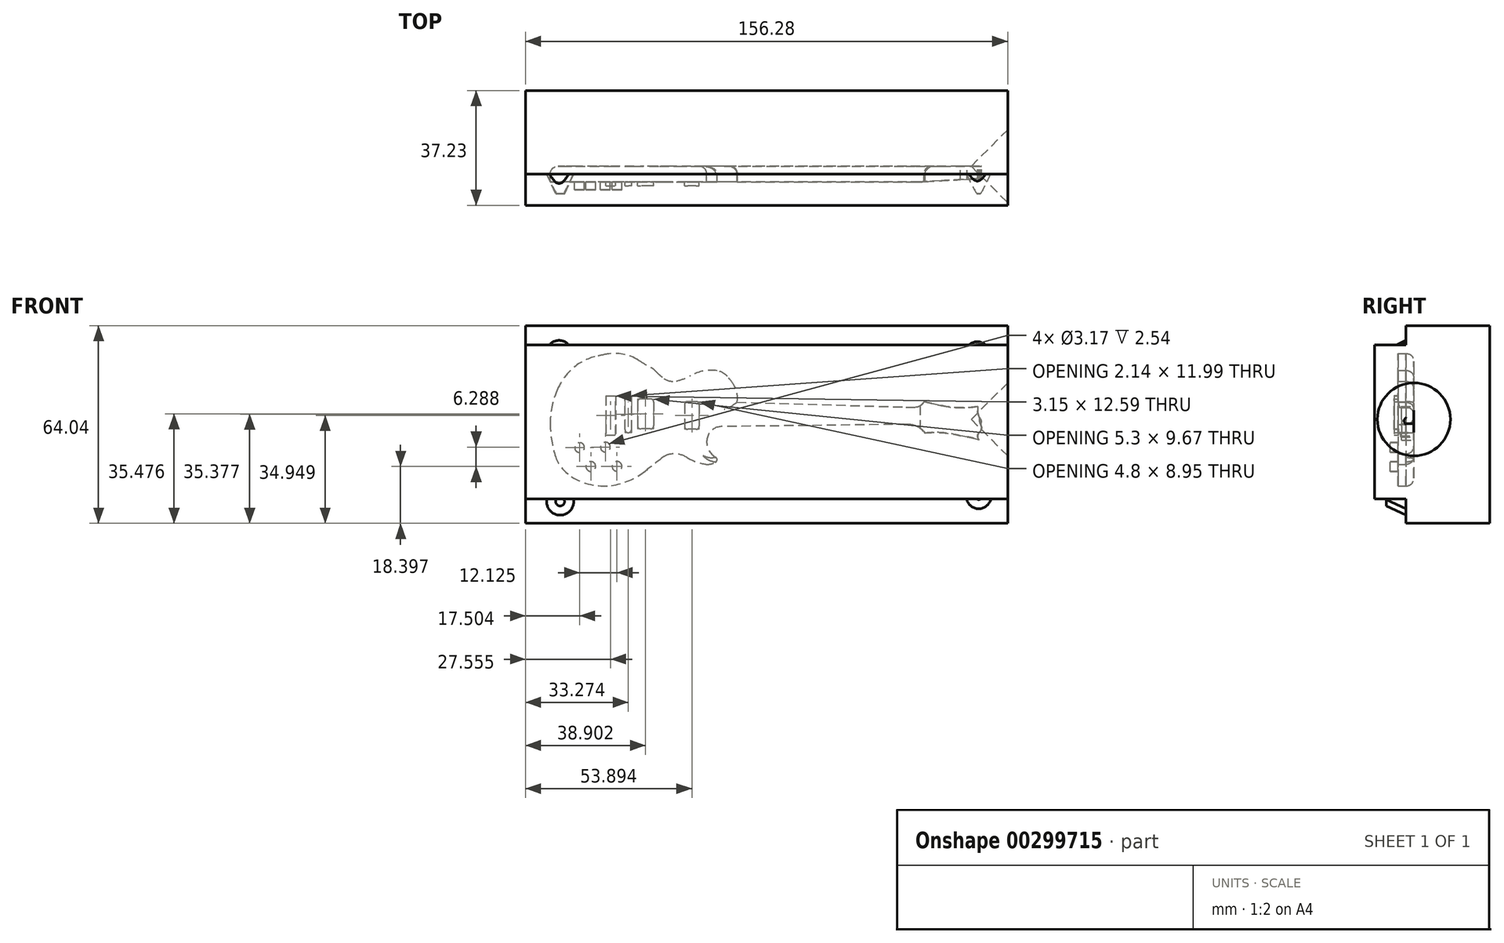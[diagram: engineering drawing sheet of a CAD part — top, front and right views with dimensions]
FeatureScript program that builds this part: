
annotation { "Feature Type Name" : "Feature", "Feature Type Description" : "" }
export const myFeature = defineFeature(function(context is Context, id is Id, definition is map)
    precondition{}
    {
        {
            var Q0;
            Q0=qCreatedBy(makeId("Front.planeOp"),FACE);
            var sketch = newSketch(context, id + "F0", { "sketchPlane" : qUnion([Q0])});
            skLineSegment(sketch, "E0", {"start": v(44.6, 23.47) * mm, "end": v(-15.58, 22.73) * mm});
            skArc(sketch, "E1", {"start": v(-15.58, 22.73) * mm, "mid": v(-18.3, 21.83) * mm, "end": v(-19.99, 19.52) * mm});
            skArc(sketch, "E2", {"start": v(-19.99, 19.52) * mm, "mid": v(-20.14, 16.5) * mm, "end": v(-18.7, 13.83) * mm});
            skArc(sketch, "E3", {"start": v(-18.7, 13.83) * mm, "mid": v(-18.05, 13.24) * mm, "end": v(-17.33, 12.73) * mm});
            skArc(sketch, "E4", {"start": v(-17.33, 12.73) * mm, "mid": v(-16.91, 12) * mm, "end": v(-17.33, 11.26) * mm});
            skArc(sketch, "E5", {"start": v(-17.33, 11.26) * mm, "mid": v(-19.1, 10.59) * mm, "end": v(-20.99, 10.58) * mm});
            skArc(sketch, "E6", {"start": v(-20.99, 10.58) * mm, "mid": v(-23.94, 11.4) * mm, "end": v(-26.69, 12.73) * mm});
            skArc(sketch, "E7", {"start": v(-26.69, 12.73) * mm, "mid": v(-29.2, 13.72) * mm, "end": v(-31.89, 13.83) * mm});
            skArc(sketch, "E8", {"start": v(-31.89, 13.83) * mm, "mid": v(-33.29, 13.46) * mm, "end": v(-34.54, 12.73) * mm});
            skArc(sketch, "E9", {"start": v(-34.54, 12.73) * mm, "mid": v(-37.37, 10.54) * mm, "end": v(-40.17, 8.33) * mm});
            skArc(sketch, "E10", {"start": v(-40.17, 8.33) * mm, "mid": v(-45.36, 5.24) * mm, "end": v(-51.18, 3.65) * mm});
            skArc(sketch, "E11", {"start": v(-51.18, 3.65) * mm, "mid": v(-57.9, 3.92) * mm, "end": v(-64.12, 6.5) * mm});
            skArc(sketch, "E12", {"start": v(-64.12, 6.5) * mm, "mid": v(-67.4, 9.5) * mm, "end": v(-69.44, 13.46) * mm});
            skArc(sketch, "E13", {"start": v(-69.44, 13.46) * mm, "mid": v(-70.63, 18.73) * mm, "end": v(-71, 24.1) * mm});
            skArc(sketch, "E14", {"start": v(-71, 24.1) * mm, "mid": v(-70.37, 29.65) * mm, "end": v(-68.62, 34.93) * mm});
            skArc(sketch, "E15", {"start": v(-68.62, 34.93) * mm, "mid": v(-66.86, 38.05) * mm, "end": v(-64.58, 40.8) * mm});
            skArc(sketch, "E16", {"start": v(-64.58, 40.8) * mm, "mid": v(-60.86, 43.66) * mm, "end": v(-56.5, 45.4) * mm});
            skArc(sketch, "E17", {"start": v(-56.5, 45.4) * mm, "mid": v(-54.54, 45.84) * mm, "end": v(-52.56, 46.22) * mm});
            skArc(sketch, "E18", {"start": v(-52.56, 46.22) * mm, "mid": v(-47.34, 46.17) * mm, "end": v(-42.47, 44.3) * mm});
            skArc(sketch, "E19", {"start": v(-42.47, 44.3) * mm, "mid": v(-40.37, 43.04) * mm, "end": v(-38.25, 41.82) * mm});
            skArc(sketch, "E20", {"start": v(-38.25, 41.82) * mm, "mid": v(-37.57, 41.36) * mm, "end": v(-36.96, 40.8) * mm});
            skArc(sketch, "E21", {"start": v(-36.96, 40.8) * mm, "mid": v(-35.6, 39.5) * mm, "end": v(-34.12, 38.33) * mm});
            skArc(sketch, "E22", {"start": v(-34.12, 38.33) * mm, "mid": v(-32.23, 37.5) * mm, "end": v(-30.17, 37.5) * mm});
            skArc(sketch, "E23", {"start": v(-30.17, 37.5) * mm, "mid": v(-27.76, 38.2) * mm, "end": v(-25.5, 39.25) * mm});
            skArc(sketch, "E24", {"start": v(-25.5, 39.25) * mm, "mid": v(-21.31, 40.75) * mm, "end": v(-16.87, 40.8) * mm});
            skArc(sketch, "E25", {"start": v(-16.87, 40.8) * mm, "mid": v(-15.11, 40.21) * mm, "end": v(-13.66, 39.06) * mm});
            skArc(sketch, "E26", {"start": v(-13.66, 39.06) * mm, "mid": v(-12.5, 37.64) * mm, "end": v(-11.45, 36.13) * mm});
            skArc(sketch, "E27", {"start": v(-11.45, 36.13) * mm, "mid": v(-10.43, 33.47) * mm, "end": v(-10.45, 30.62) * mm});
            skLineSegment(sketch, "E28", {"start": v(-10.45, 30.62) * mm, "end": v(44.33, 29.06) * mm});
            skArc(sketch, "E29", {"start": v(44.33, 29.06) * mm, "mid": v(45.89, 29.04) * mm, "end": v(47.45, 29.06) * mm});
            skArc(sketch, "E30", {"start": v(47.45, 29.06) * mm, "mid": v(49.03, 29.56) * mm, "end": v(50.1, 30.8) * mm});
            skLineSegment(sketch, "E31", {"start": v(50.1, 30.8) * mm, "end": v(55.8, 29.56) * mm});
            skPoint(sketch, "E31.endSnap0", {"position": v(49.03, 29.56) * mm});
            skArc(sketch, "E32", {"start": v(55.8, 29.56) * mm, "mid": v(61.65, 28.84) * mm, "end": v(67.54, 29.25) * mm});
            skLineSegment(sketch, "E33", {"start": v(67.54, 29.25) * mm, "end": v(67.54, 28) * mm});
            skArc(sketch, "E34", {"start": v(67.54, 28) * mm, "mid": v(67.78, 26.48) * mm, "end": v(68.47, 25.1) * mm});
            skArc(sketch, "E35", {"start": v(68.47, 25.1) * mm, "mid": v(68.7, 24.38) * mm, "end": v(68.47, 23.66) * mm});
            skLineSegment(sketch, "E36", {"start": v(68.47, 23.66) * mm, "end": v(68.7, 22.95) * mm});
            skPoint(sketch, "E36.endSnap0", {"position": v(68.7, 24.38) * mm});
            skArc(sketch, "E37", {"start": v(68.7, 22.95) * mm, "mid": v(68.72, 21.86) * mm, "end": v(68.15, 20.94) * mm});
            skArc(sketch, "E38", {"start": v(68.15, 20.94) * mm, "mid": v(67.53, 19.62) * mm, "end": v(68.08, 18.28) * mm});
            skLineSegment(sketch, "E39", {"start": v(68.08, 18.28) * mm, "end": v(66.46, 18.86) * mm});
            skArc(sketch, "E40", {"start": v(66.46, 18.86) * mm, "mid": v(65.3, 19.2) * mm, "end": v(64.12, 19.38) * mm});
            skArc(sketch, "E41", {"start": v(61.92, 19.77) * mm, "mid": v(56.25, 20.73) * mm, "end": v(50.5, 20.68) * mm});
            skLineSegment(sketch, "E42", {"start": v(64.12, 19.38) * mm, "end": v(61.92, 19.77) * mm});
            skArc(sketch, "E43", {"start": v(44.6, 23.47) * mm, "mid": v(47.87, 22.75) * mm, "end": v(50.5, 20.68) * mm});
            skPoint(sketch, "E44", {"position": v(-15.58, 22.73) * mm});
            skSolve(sketch);
        }
        {
            var Q0;
            Q0=qSketchRegion(id+"F0",true);
            extrude(context, id + "F1", {"entities" : qUnion([Q0]), "depth" : 5.08 * mm});
        }
        {
            var Q0;
            Q0=makeQuery(id+"F1.opExtrude","CAP_FACE",FACE,{"disambiguationData":[OSD([sQuery(id+"F0.wireOp",EDGE,"E0"),sQuery(id+"F0.wireOp",EDGE,"E1"),sQuery(id+"F0.wireOp",EDGE,"E2"),sQuery(id+"F0.wireOp",EDGE,"E3"),sQuery(id+"F0.wireOp",EDGE,"E4"),sQuery(id+"F0.wireOp",EDGE,"E5"),sQuery(id+"F0.wireOp",EDGE,"E6"),sQuery(id+"F0.wireOp",EDGE,"E7"),sQuery(id+"F0.wireOp",EDGE,"E8"),sQuery(id+"F0.wireOp",EDGE,"E9"),sQuery(id+"F0.wireOp",EDGE,"E10"),sQuery(id+"F0.wireOp",EDGE,"E11"),sQuery(id+"F0.wireOp",EDGE,"E12"),sQuery(id+"F0.wireOp",EDGE,"E13"),sQuery(id+"F0.wireOp",EDGE,"E14"),sQuery(id+"F0.wireOp",EDGE,"E15"),sQuery(id+"F0.wireOp",EDGE,"E16"),sQuery(id+"F0.wireOp",EDGE,"E17"),sQuery(id+"F0.wireOp",EDGE,"E18"),sQuery(id+"F0.wireOp",EDGE,"E19"),sQuery(id+"F0.wireOp",EDGE,"E20"),sQuery(id+"F0.wireOp",EDGE,"E21"),sQuery(id+"F0.wireOp",EDGE,"E22"),sQuery(id+"F0.wireOp",EDGE,"E23"),sQuery(id+"F0.wireOp",EDGE,"E24"),sQuery(id+"F0.wireOp",EDGE,"E25"),sQuery(id+"F0.wireOp",EDGE,"E26"),sQuery(id+"F0.wireOp",EDGE,"E27"),sQuery(id+"F0.wireOp",EDGE,"E28"),sQuery(id+"F0.wireOp",EDGE,"E29"),sQuery(id+"F0.wireOp",EDGE,"E30"),sQuery(id+"F0.wireOp",EDGE,"E31"),sQuery(id+"F0.wireOp",EDGE,"E32"),sQuery(id+"F0.wireOp",EDGE,"E33"),sQuery(id+"F0.wireOp",EDGE,"E34"),sQuery(id+"F0.wireOp",EDGE,"E35"),sQuery(id+"F0.wireOp",EDGE,"E36"),sQuery(id+"F0.wireOp",EDGE,"E37"),sQuery(id+"F0.wireOp",EDGE,"E38"),sQuery(id+"F0.wireOp",EDGE,"E39"),sQuery(id+"F0.wireOp",EDGE,"E40"),sQuery(id+"F0.wireOp",EDGE,"E41"),sQuery(id+"F0.wireOp",EDGE,"E42"),sQuery(id+"F0.wireOp",EDGE,"E43")])],"isStart":false});
            var sketch = newSketch(context, id + "F2", { "sketchPlane" : qUnion([Q0])});
            skLineSegment(sketch, "E45.bottom", {"start": v(-22.7, 30.81) * mm, "end": v(-27.5, 30.81) * mm});
            skLineSegment(sketch, "E45.top", {"start": v(-22.7, 21.87) * mm, "end": v(-27.5, 21.87) * mm});
            skLineSegment(sketch, "E45.left", {"start": v(-22.7, 30.81) * mm, "end": v(-22.7, 21.87) * mm});
            skLineSegment(sketch, "E45.right", {"start": v(-27.5, 30.81) * mm, "end": v(-27.5, 21.87) * mm});
            skLineSegment(sketch, "E46.bottom", {"start": v(-37.44, 31.7) * mm, "end": v(-42.74, 31.7) * mm});
            skLineSegment(sketch, "E46.top", {"start": v(-37.44, 22.03) * mm, "end": v(-42.74, 22.03) * mm});
            skLineSegment(sketch, "E46.left", {"start": v(-37.44, 31.7) * mm, "end": v(-37.44, 22.03) * mm});
            skLineSegment(sketch, "E46.right", {"start": v(-42.74, 31.7) * mm, "end": v(-42.74, 22.03) * mm});
            skLineSegment(sketch, "E47.bottom", {"start": v(-53, 32.63) * mm, "end": v(-49.86, 32.63) * mm});
            skLineSegment(sketch, "E47.top", {"start": v(-53, 20.04) * mm, "end": v(-49.86, 20.04) * mm});
            skLineSegment(sketch, "E47.left", {"start": v(-53, 32.63) * mm, "end": v(-53, 20.04) * mm});
            skLineSegment(sketch, "E47.right", {"start": v(-49.86, 32.63) * mm, "end": v(-49.86, 20.04) * mm});
            skLineSegment(sketch, "E48.bottom", {"start": v(-46.78, 20.77) * mm, "end": v(-44.65, 20.77) * mm});
            skLineSegment(sketch, "E48.top", {"start": v(-46.78, 32.76) * mm, "end": v(-44.65, 32.76) * mm});
            skLineSegment(sketch, "E48.left", {"start": v(-46.78, 20.77) * mm, "end": v(-46.78, 32.76) * mm});
            skLineSegment(sketch, "E48.right", {"start": v(-44.65, 20.77) * mm, "end": v(-44.65, 32.76) * mm});
            skSolve(sketch);
        }
        {
            var Q0;
            Q0=qSketchRegion(id+"F2",true);
            extrude(context, id + "F3", {"entities" : qUnion([Q0]), "operationType" : NewBodyOperationType.ADD, "depth" : 1.27 * mm});
        }
        {
            var Q0;
            Q0=makeQuery(id+"F2.imprint","IMPRINT",FACE,{"disambiguationData":[TD([[makeQuery(id+"F2.imprint","IMPRINT",EDGE,{"derivedFrom":sQuery(id+"F2.wireOp",EDGE,"E45.bottom")}),-1.0]])]});
            var sketch = newSketch(context, id + "F4", { "sketchPlane" : qUnion([Q0])});
            skCircle(sketch, "E49", {"center": v(-61.49, 15.93) * mm, "radius": 1.59 * mm});
            skPoint(sketch, "E49.first.point", {"position": v(-60.6, 17.25) * mm});
            skPoint(sketch, "E49.second.point", {"position": v(-63.06, 15.77) * mm});
            skPoint(sketch, "E49.third.point", {"position": v(-60.92, 14.45) * mm});
            skCircle(sketch, "E50", {"center": v(-53.12, 16.07) * mm, "radius": 1.59 * mm});
            skPoint(sketch, "E50.first.point", {"position": v(-54.4, 17.02) * mm});
            skPoint(sketch, "E50.second.point", {"position": v(-51.54, 16.26) * mm});
            skPoint(sketch, "E50.third.point", {"position": v(-51.7, 15.34) * mm});
            skCircle(sketch, "E51", {"center": v(-49.36, 9.85) * mm, "radius": 1.59 * mm});
            skPoint(sketch, "E51.first.point", {"position": v(-50.38, 11.07) * mm});
            skPoint(sketch, "E51.second.point", {"position": v(-48.35, 8.62) * mm});
            skPoint(sketch, "E51.third.point", {"position": v(-50.52, 8.76) * mm});
            skCircle(sketch, "E52", {"center": v(-57.85, 9.79) * mm, "radius": 1.59 * mm});
            skPoint(sketch, "E52.first.point", {"position": v(-57.26, 8.31) * mm});
            skPoint(sketch, "E52.second.point", {"position": v(-58.38, 11.29) * mm});
            skPoint(sketch, "E52.third.point", {"position": v(-59.42, 9.5) * mm});
            skSolve(sketch);
        }
        {
            var Q0;
            Q0=qSketchRegion(id+"F4",true);
            extrude(context, id + "F5", {"entities" : qUnion([Q0]), "operationType" : NewBodyOperationType.ADD, "depth" : 2.54 * mm});
        }
        {
            var Q0;
            Q0=makeQuery(id+"F1.opExtrude","CAP_EDGE",EDGE,{"disambiguationData":[OSD([sQuery(id+"F0.wireOp",EDGE,"E0")])],"isStart":true});
            var Q1;
            Q1=makeQuery(id+"F1.opExtrude","CAP_EDGE",EDGE,{"disambiguationData":[OSD([sQuery(id+"F0.wireOp",EDGE,"E28")])],"isStart":true});
            fillet(context, id + "F6", {"entities" : qUnion([Q0, Q1]), "radius" : 2.54 * mm, "tangentPropagation" : true, "allowEdgeOverflow" : false});
        }
        {
            var Q0;
            Q0=qCreatedBy(makeId("Top.planeOp"),FACE);
            var sketch = newSketch(context, id + "F7", { "sketchPlane" : qUnion([Q0])});
            skLineSegment(sketch, "E53", {"start": v(39.16, -5.62) * mm, "end": v(72.7, -3.75) * mm});
            skLineSegment(sketch, "E54", {"start": v(72.7, -3.75) * mm, "end": v(71.44, -9.77) * mm});
            skLineSegment(sketch, "E55", {"start": v(71.44, -9.77) * mm, "end": v(39.16, -5.62) * mm});
            skSolve(sketch);
        }
        {
            var Q0;
            Q0=makeQuery(id+"F7.imprint","IMPRINT",FACE,{"disambiguationData":[TD([[makeQuery(id+"F7.imprint","IMPRINT",EDGE,{"derivedFrom":sQuery(id+"F7.wireOp",EDGE,"E53")}),-1.0]])]});
            extrude(context, id + "F8", {"entities" : qUnion([Q0]), "operationType" : NewBodyOperationType.REMOVE, "depth" : 50.8 * mm});
        }
        {
            var Q0;
            Q0=makeQuery(id+"F3.opExtrude","SWEPT_EDGE",EDGE,{"disambiguationData":[OSD([sQuery(id+"F2.wireOp",EDGE,"E48.top"),sQuery(id+"F2.wireOp",EDGE,"E48.right")])]});
            var Q1;
            Q1=makeQuery(id+"F3.opExtrude","SWEPT_EDGE",EDGE,{"disambiguationData":[OSD([sQuery(id+"F2.wireOp",EDGE,"E48.top"),sQuery(id+"F2.wireOp",EDGE,"E48.left")])]});
            var Q2;
            Q2=makeQuery(id+"F3.opExtrude","SWEPT_EDGE",EDGE,{"disambiguationData":[OSD([sQuery(id+"F2.wireOp",EDGE,"E48.bottom"),sQuery(id+"F2.wireOp",EDGE,"E48.left")])]});
            var Q3;
            Q3=makeQuery(id+"F3.opExtrude","SWEPT_EDGE",EDGE,{"disambiguationData":[OSD([sQuery(id+"F2.wireOp",EDGE,"E48.bottom"),sQuery(id+"F2.wireOp",EDGE,"E48.right")])]});
            fillet(context, id + "F9", {"entities" : qUnion([Q0, Q1, Q2, Q3]), "radius" : 1.02 * mm, "tangentPropagation" : true, "allowEdgeOverflow" : false});
        }
        {
            var Q0;
            Q0=makeQuery(id+"F3.opExtrude","SWEPT_EDGE",EDGE,{"disambiguationData":[OSD([sQuery(id+"F2.wireOp",EDGE,"E46.bottom"),sQuery(id+"F2.wireOp",EDGE,"E46.left")])]});
            var Q1;
            Q1=makeQuery(id+"F3.opExtrude","SWEPT_EDGE",EDGE,{"disambiguationData":[OSD([sQuery(id+"F2.wireOp",EDGE,"E46.bottom"),sQuery(id+"F2.wireOp",EDGE,"E46.right")])]});
            var Q2;
            Q2=makeQuery(id+"F3.opExtrude","SWEPT_EDGE",EDGE,{"disambiguationData":[OSD([sQuery(id+"F2.wireOp",EDGE,"E46.top"),sQuery(id+"F2.wireOp",EDGE,"E46.right")])]});
            var Q3;
            Q3=makeQuery(id+"F3.opExtrude","SWEPT_EDGE",EDGE,{"disambiguationData":[OSD([sQuery(id+"F2.wireOp",EDGE,"E46.top"),sQuery(id+"F2.wireOp",EDGE,"E46.left")])]});
            var Q4;
            Q4=makeQuery(id+"F3.opExtrude","SWEPT_EDGE",EDGE,{"disambiguationData":[OSD([sQuery(id+"F2.wireOp",EDGE,"E45.top"),sQuery(id+"F2.wireOp",EDGE,"E45.left")])]});
            var Q5;
            Q5=makeQuery(id+"F3.opExtrude","SWEPT_EDGE",EDGE,{"disambiguationData":[OSD([sQuery(id+"F2.wireOp",EDGE,"E45.top"),sQuery(id+"F2.wireOp",EDGE,"E45.right")])]});
            var Q6;
            Q6=makeQuery(id+"F3.opExtrude","SWEPT_EDGE",EDGE,{"disambiguationData":[OSD([sQuery(id+"F2.wireOp",EDGE,"E45.bottom"),sQuery(id+"F2.wireOp",EDGE,"E45.right")])]});
            var Q7;
            Q7=makeQuery(id+"F3.opExtrude","SWEPT_EDGE",EDGE,{"disambiguationData":[OSD([sQuery(id+"F2.wireOp",EDGE,"E45.bottom"),sQuery(id+"F2.wireOp",EDGE,"E45.left")])]});
            fillet(context, id + "F10", {"entities" : qUnion([Q0, Q1, Q2, Q3, Q4, Q5, Q6, Q7]), "radius" : 1.02 * mm, "tangentPropagation" : true, "allowEdgeOverflow" : false});
        }
        {
            var Q0;
            Q0=makeQuery(id+"F1.opExtrude","CAP_FACE",FACE,{"disambiguationData":[OSD([sQuery(id+"F0.wireOp",EDGE,"E0"),sQuery(id+"F0.wireOp",EDGE,"E1"),sQuery(id+"F0.wireOp",EDGE,"E2"),sQuery(id+"F0.wireOp",EDGE,"E3"),sQuery(id+"F0.wireOp",EDGE,"E4"),sQuery(id+"F0.wireOp",EDGE,"E5"),sQuery(id+"F0.wireOp",EDGE,"E6"),sQuery(id+"F0.wireOp",EDGE,"E7"),sQuery(id+"F0.wireOp",EDGE,"E8"),sQuery(id+"F0.wireOp",EDGE,"E9"),sQuery(id+"F0.wireOp",EDGE,"E10"),sQuery(id+"F0.wireOp",EDGE,"E11"),sQuery(id+"F0.wireOp",EDGE,"E12"),sQuery(id+"F0.wireOp",EDGE,"E13"),sQuery(id+"F0.wireOp",EDGE,"E14"),sQuery(id+"F0.wireOp",EDGE,"E15"),sQuery(id+"F0.wireOp",EDGE,"E16"),sQuery(id+"F0.wireOp",EDGE,"E17"),sQuery(id+"F0.wireOp",EDGE,"E18"),sQuery(id+"F0.wireOp",EDGE,"E19"),sQuery(id+"F0.wireOp",EDGE,"E20"),sQuery(id+"F0.wireOp",EDGE,"E21"),sQuery(id+"F0.wireOp",EDGE,"E22"),sQuery(id+"F0.wireOp",EDGE,"E23"),sQuery(id+"F0.wireOp",EDGE,"E24"),sQuery(id+"F0.wireOp",EDGE,"E25"),sQuery(id+"F0.wireOp",EDGE,"E26"),sQuery(id+"F0.wireOp",EDGE,"E27"),sQuery(id+"F0.wireOp",EDGE,"E28"),sQuery(id+"F0.wireOp",EDGE,"E29"),sQuery(id+"F0.wireOp",EDGE,"E30"),sQuery(id+"F0.wireOp",EDGE,"E31"),sQuery(id+"F0.wireOp",EDGE,"E32"),sQuery(id+"F0.wireOp",EDGE,"E33"),sQuery(id+"F0.wireOp",EDGE,"E34"),sQuery(id+"F0.wireOp",EDGE,"E35"),sQuery(id+"F0.wireOp",EDGE,"E36"),sQuery(id+"F0.wireOp",EDGE,"E37"),sQuery(id+"F0.wireOp",EDGE,"E38"),sQuery(id+"F0.wireOp",EDGE,"E39"),sQuery(id+"F0.wireOp",EDGE,"E40"),sQuery(id+"F0.wireOp",EDGE,"E41"),sQuery(id+"F0.wireOp",EDGE,"E42"),sQuery(id+"F0.wireOp",EDGE,"E43")])],"isStart":true});
            var sketch = newSketch(context, id + "F11", { "sketchPlane" : qUnion([Q0])});
            skLineSegment(sketch, "E56.bottom", {"start": v(78.99, -0.76) * mm, "end": v(-77.3, -0.76) * mm});
            skLineSegment(sketch, "E56.top", {"start": v(78.99, 49.22) * mm, "end": v(-77.3, 49.22) * mm});
            skLineSegment(sketch, "E56.left", {"start": v(78.99, -0.76) * mm, "end": v(78.99, 49.22) * mm});
            skLineSegment(sketch, "E56.right", {"start": v(-77.3, -0.76) * mm, "end": v(-77.3, 49.22) * mm});
            skSolve(sketch);
        }
        {
            var Q0;
            Q0 = qSketchRegion(id + "F11", true);
            extrude(context, id + "F12", {"entities" : qUnion([Q0]), "endBound" : BoundingType.SYMMETRIC, "depth" : 25.4 * mm});
        }
        {
            var Q0;
            Q0=makeQuery(id+"F1.opExtrude","SWEPT_BODY",BODY,{"disambiguationData":[OSD([sQuery(id+"F0.wireOp",EDGE,"E0"),sQuery(id+"F0.wireOp",EDGE,"E1"),sQuery(id+"F0.wireOp",EDGE,"E2"),sQuery(id+"F0.wireOp",EDGE,"E3"),sQuery(id+"F0.wireOp",EDGE,"E4"),sQuery(id+"F0.wireOp",EDGE,"E5"),sQuery(id+"F0.wireOp",EDGE,"E6"),sQuery(id+"F0.wireOp",EDGE,"E7"),sQuery(id+"F0.wireOp",EDGE,"E8"),sQuery(id+"F0.wireOp",EDGE,"E9"),sQuery(id+"F0.wireOp",EDGE,"E10"),sQuery(id+"F0.wireOp",EDGE,"E11"),sQuery(id+"F0.wireOp",EDGE,"E12"),sQuery(id+"F0.wireOp",EDGE,"E13"),sQuery(id+"F0.wireOp",EDGE,"E14"),sQuery(id+"F0.wireOp",EDGE,"E15"),sQuery(id+"F0.wireOp",EDGE,"E16"),sQuery(id+"F0.wireOp",EDGE,"E17"),sQuery(id+"F0.wireOp",EDGE,"E18"),sQuery(id+"F0.wireOp",EDGE,"E19"),sQuery(id+"F0.wireOp",EDGE,"E20"),sQuery(id+"F0.wireOp",EDGE,"E21"),sQuery(id+"F0.wireOp",EDGE,"E22"),sQuery(id+"F0.wireOp",EDGE,"E23"),sQuery(id+"F0.wireOp",EDGE,"E24"),sQuery(id+"F0.wireOp",EDGE,"E25"),sQuery(id+"F0.wireOp",EDGE,"E26"),sQuery(id+"F0.wireOp",EDGE,"E27"),sQuery(id+"F0.wireOp",EDGE,"E28"),sQuery(id+"F0.wireOp",EDGE,"E29"),sQuery(id+"F0.wireOp",EDGE,"E30"),sQuery(id+"F0.wireOp",EDGE,"E31"),sQuery(id+"F0.wireOp",EDGE,"E32"),sQuery(id+"F0.wireOp",EDGE,"E33"),sQuery(id+"F0.wireOp",EDGE,"E34"),sQuery(id+"F0.wireOp",EDGE,"E35"),sQuery(id+"F0.wireOp",EDGE,"E36"),sQuery(id+"F0.wireOp",EDGE,"E37"),sQuery(id+"F0.wireOp",EDGE,"E38"),sQuery(id+"F0.wireOp",EDGE,"E39"),sQuery(id+"F0.wireOp",EDGE,"E40"),sQuery(id+"F0.wireOp",EDGE,"E41"),sQuery(id+"F0.wireOp",EDGE,"E42"),sQuery(id+"F0.wireOp",EDGE,"E43")])]});
            var Q1;
            Q1=makeQuery(id+"F12.opExtrude","SWEPT_BODY",BODY,{"disambiguationData":[OSD([sQuery(id+"F11.wireOp",EDGE,"E56.bottom"),sQuery(id+"F11.wireOp",EDGE,"E56.top"),sQuery(id+"F11.wireOp",EDGE,"E56.left"),sQuery(id+"F11.wireOp",EDGE,"E56.right")])]});
            booleanBodies(context, id + "F13", {"operationType" : BooleanOperationType.SUBTRACTION, "tools" : qUnion([Q0]), "targets" : qUnion([Q1]), "keepTools" : true});
        }
        {
            var Q0;
            Q0=makeQuery(id+"F12.opExtrude","SWEPT_FACE",FACE,{"disambiguationData":[OSD([sQuery(id+"F11.wireOp",EDGE,"E56.right")])]});
            var sketch = newSketch(context, id + "F14", { "sketchPlane" : qUnion([Q0])});
            skPoint(sketch, "E57.0", {"position": v(-2, 23.66) * mm});
            skCircle(sketch, "E58", {"center": v(-2, 23.66) * mm, "radius": 8.6 * mm});
            skSolve(sketch);
        }
        {
            var Q0;
            Q0=makeQuery(id+"F14.imprint","IMPRINT",FACE,{"disambiguationData":[TD([[makeQuery(id+"F14.imprint","IMPRINT",EDGE,{"derivedFrom":sQuery(id+"F14.wireOp",EDGE,"E58")}),-1.0]])]});
            cPlane(context, id + "F15", {"entities" : qUnion([Q0]), "cplaneType" : CPlaneType.OFFSET, "offset" : 12.7 * mm, "oppositeDirection" : true, "width" : 152.4 * mm, "height" : 152.4 * mm});
        }
        {
            var Q0;
            Q0=makeQuery(id+"F12.opExtrude","SWEPT_FACE",FACE,{"disambiguationData":[OSD([sQuery(id+"F11.wireOp",EDGE,"E56.left")])]});
            var sketch = newSketch(context, id + "F16", { "sketchPlane" : qUnion([Q0])});
            skPoint(sketch, "E59.0", {"position": v(2.54, 3.65) * mm});
            skPoint(sketch, "E60.0", {"position": v(2.54, 46.22) * mm});
            skLineSegment(sketch, "E61.bottom", {"start": v(-24.53, -8.61) * mm, "end": v(2.54, -8.61) * mm});
            skLineSegment(sketch, "E61.top", {"start": v(-24.53, 55.43) * mm, "end": v(2.54, 55.43) * mm});
            skLineSegment(sketch, "E61.left", {"start": v(-24.53, -8.61) * mm, "end": v(-24.53, 55.43) * mm});
            skLineSegment(sketch, "E61.right", {"start": v(2.54, -8.61) * mm, "end": v(2.54, 55.43) * mm});
            skSolve(sketch);
        }
        {
            var Q0;
            {var subQ1=sQuery(id+"F11.wireOp",EDGE,"E56.left");var subQ6=makeQuery(id+"F12.opExtrude","CAP_EDGE",EDGE,{"disambiguationData":[OSD([subQ1])],"isStart":false});Q0=makeQuery(id+"F16.imprint","IMPRINT",FACE,{"disambiguationData":[TD([[makeQuery(id+"F16.imprint","IMPRINT",EDGE,{"derivedFrom":subQ6}),-1.0]])]});}
            var Q1;
            {var subQ1=sQuery(id+"F16.wireOp",EDGE,"E61.bottom");Q1=makeQuery(id+"F16.imprint","IMPRINT",FACE,{"disambiguationData":[TD([[makeQuery(id+"F16.imprint","IMPRINT",EDGE,{"derivedFrom":subQ1}),1.0]])]});}
            var Q2;
            Q2=makeQuery(id+"F12.opExtrude","SWEPT_FACE",FACE,{"disambiguationData":[OSD([sQuery(id+"F11.wireOp",EDGE,"E56.right")])]});
            extrude(context, id + "F17", {"entities" : qUnion([Q0, Q1]), "endBound" : BoundingType.UP_TO_SURFACE, "oppositeDirection" : true, "endBoundEntityFace" : qUnion([Q2]), "depth" : 25.4 * mm});
        }
        {
            var Q0;
            Q0=makeQuery(id+"F17.opExtrude","SWEPT_FACE",FACE,{"disambiguationData":[OSD([sQuery(id+"F16.wireOp",EDGE,"E61.right")])]});
            var sketch = newSketch(context, id + "F18", { "sketchPlane" : qUnion([Q0])});
            skCircle(sketch, "E62", {"center": v(67.88, 0.1) * mm, "radius": 4 * mm});
            skCircle(sketch, "E63", {"center": v(67.44, 46.28) * mm, "radius": 4 * mm});
            skCircle(sketch, "E64", {"center": v(-3, 7.83) * mm, "radius": 4.44 * mm});
            skCircle(sketch, "E65", {"center": v(-4.56, 44.02) * mm, "radius": 4.62 * mm});
            skCircle(sketch, "E66", {"center": v(-67.8, -1.57) * mm, "radius": 4.4 * mm});
            skCircle(sketch, "E67", {"center": v(-68.14, 46.6) * mm, "radius": 4.08 * mm});
            skSolve(sketch);
        }
        {
            var Q0;
            Q0=makeQuery(id+"F18.imprint","IMPRINT",FACE,{"disambiguationData":[TD([[makeQuery(id+"F18.imprint","IMPRINT",EDGE,{"derivedFrom":sQuery(id+"F18.wireOp",EDGE,"E67")}),1.0]])]});
            var Q1;
            Q1=makeQuery(id+"F18.imprint","IMPRINT",FACE,{"disambiguationData":[TD([[makeQuery(id+"F18.imprint","IMPRINT",EDGE,{"derivedFrom":sQuery(id+"F18.wireOp",EDGE,"E65")}),1.0]])]});
            var Q2;
            Q2=makeQuery(id+"F18.imprint","IMPRINT",FACE,{"disambiguationData":[TD([[makeQuery(id+"F18.imprint","IMPRINT",EDGE,{"derivedFrom":sQuery(id+"F18.wireOp",EDGE,"E64")}),1.0]])]});
            var Q3;
            Q3=makeQuery(id+"F18.imprint","IMPRINT",FACE,{"disambiguationData":[TD([[makeQuery(id+"F18.imprint","IMPRINT",EDGE,{"derivedFrom":sQuery(id+"F18.wireOp",EDGE,"E63")}),1.0]])]});
            var Q4;
            Q4=makeQuery(id+"F18.imprint","IMPRINT",FACE,{"disambiguationData":[TD([[makeQuery(id+"F18.imprint","IMPRINT",EDGE,{"derivedFrom":sQuery(id+"F18.wireOp",EDGE,"E62")}),1.0]])]});
            var Q5;
            Q5=makeQuery(id+"F18.imprint","IMPRINT",FACE,{"disambiguationData":[TD([[makeQuery(id+"F18.imprint","IMPRINT",EDGE,{"derivedFrom":sQuery(id+"F18.wireOp",EDGE,"E66")}),1.0]])]});
            extrude(context, id + "F19", {"entities" : qUnion([Q0, Q1, Q2, Q3, Q4, Q5]), "operationType" : NewBodyOperationType.ADD, "depth" : 6.35 * mm, "hasDraft" : true, "draftAngle" : 25 * degree, "draftPullDirection" : true});
        }
        {
            var Q0;
            Q0=makeQuery(id+"F17.opExtrude","CAP_FACE",FACE,{"disambiguationData":[OSD([sQuery(id+"F16.wireOp",EDGE,"E61.bottom"),sQuery(id+"F16.wireOp",EDGE,"E61.top"),sQuery(id+"F16.wireOp",EDGE,"E61.left"),sQuery(id+"F16.wireOp",EDGE,"E61.right")])],"isStart":false});
            var sketch = newSketch(context, id + "F20", { "sketchPlane" : qUnion([Q0])});
            skPoint(sketch, "E68.0", {"position": v(0, 25.1) * mm});
            skCircle(sketch, "E69", {"center": v(0, 25.1) * mm, "radius": 11.83 * mm});
            skSolve(sketch);
        }
        {
            var Q0;
            Q0 = qSketchRegion(id + "F20", true);
            extrude(context, id + "F21", {"entities" : qUnion([Q0]), "oppositeDirection" : true, "depth" : 25.4 * mm, "hasDraft" : true, "draftAngle" : 45 * degree, "draftPullDirection" : true});
        }
        {
            var Q0;
            Q0=makeQuery(id+"F17.opExtrude","SWEPT_BODY",BODY,{"disambiguationData":[OSD([sQuery(id+"F16.wireOp",EDGE,"E61.bottom"),sQuery(id+"F16.wireOp",EDGE,"E61.top"),sQuery(id+"F16.wireOp",EDGE,"E61.left"),sQuery(id+"F16.wireOp",EDGE,"E61.right")])]});
            var Q1;
            Q1=makeQuery(id+"F21.opExtrude","SWEPT_BODY",BODY,{"disambiguationData":[OSD([sQuery(id+"F20.wireOp",EDGE,"E69")])]});
            var Q2;
            Q2=makeQuery(id+"F12.opExtrude","SWEPT_BODY",BODY,{"disambiguationData":[OSD([sQuery(id+"F11.wireOp",EDGE,"E56.bottom"),sQuery(id+"F11.wireOp",EDGE,"E56.top"),sQuery(id+"F11.wireOp",EDGE,"E56.left"),sQuery(id+"F11.wireOp",EDGE,"E56.right")])]});
            booleanBodies(context, id + "F22", {"operationType" : BooleanOperationType.SUBTRACTION, "tools" : qUnion([Q0, Q1]), "targets" : qUnion([Q2])});
        }
    });
